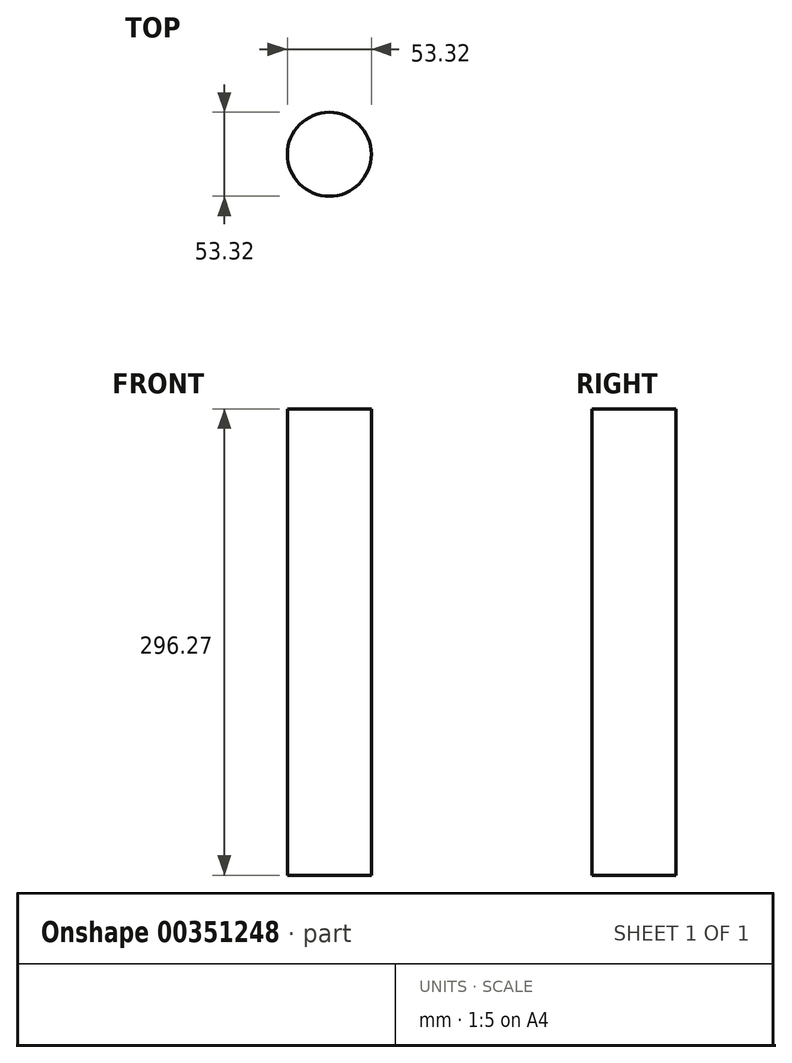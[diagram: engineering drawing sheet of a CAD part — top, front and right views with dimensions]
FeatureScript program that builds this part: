
annotation { "Feature Type Name" : "Feature", "Feature Type Description" : "" }
export const myFeature = defineFeature(function(context is Context, id is Id, definition is map)
    precondition{}
    {
        {
            var Q0;
            Q0=qCreatedBy(makeId("Front.planeOp"),FACE);
            var sketch = newSketch(context, id + "F0", { "sketchPlane" : qUnion([Q0])});
            skLineSegment(sketch, "E0", {"start": v(0, 0) * mm, "end": v(0, 296.27) * mm});
            skLineSegment(sketch, "E1", {"start": v(0, 296.27) * mm, "end": v(26.66, 296.27) * mm});
            skLineSegment(sketch, "E2", {"start": v(26.66, 296.27) * mm, "end": v(26.66, 0) * mm});
            skLineSegment(sketch, "E3", {"start": v(26.66, 0) * mm, "end": v(0, 0) * mm});
            skLineSegment(sketch, "E4", {"start": v(0, -75.85) * mm, "end": v(0, 374.02) * mm, "construction": true});
            skSolve(sketch);
        }
        {
            var Q0;
            Q0=makeQuery(id+"F0.imprint","IMPRINT",FACE,{"disambiguationData":[TD([[makeQuery(id+"F0.imprint","IMPRINT",EDGE,{"derivedFrom":sQuery(id+"F0.wireOp",EDGE,"E0")}),-1.0]])]});
            var Q1;
            Q1=sQuery(id+"F0.wireOp",EDGE,"E4");
            revolve(context, id + "F1", {"entities" : qUnion([Q0]), "axis" : qUnion([Q1]), "revolveType" : RevolveType.FULL});
        }
    });
